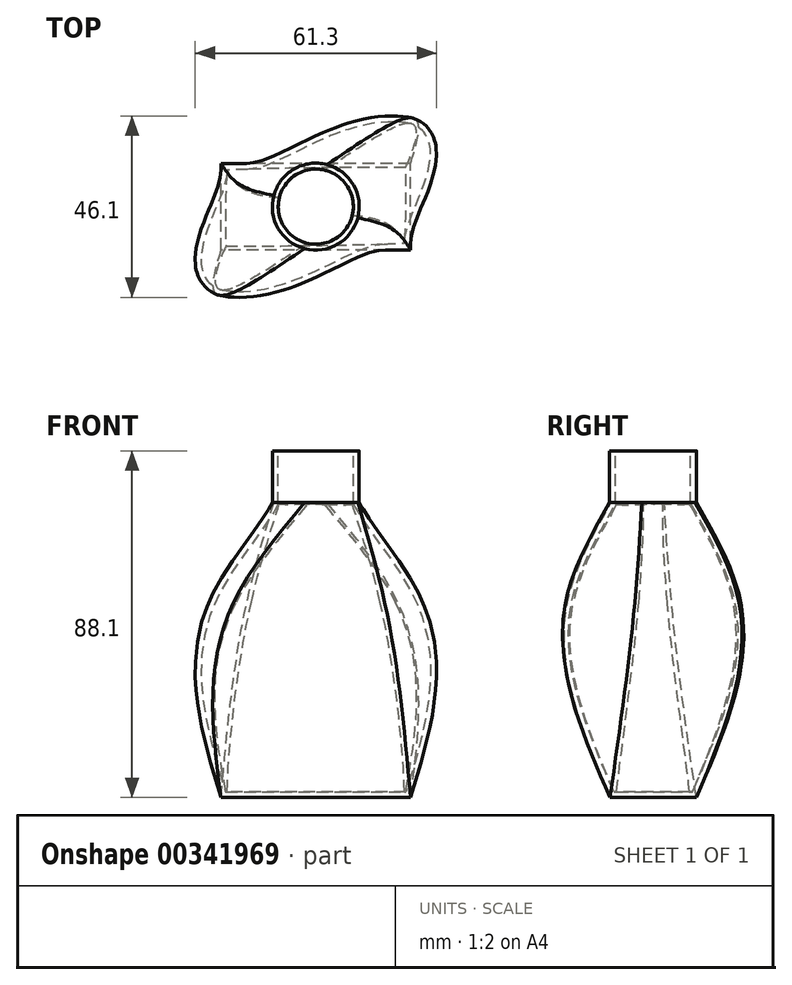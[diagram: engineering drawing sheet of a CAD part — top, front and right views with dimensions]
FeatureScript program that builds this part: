
annotation { "Feature Type Name" : "Feature", "Feature Type Description" : "" }
export const myFeature = defineFeature(function(context is Context, id is Id, definition is map)
    precondition{}
    {
        {
            var Q0;
            Q0=qCreatedBy(makeId("Top.planeOp"),FACE);
            var sketch = newSketch(context, id + "F0", { "sketchPlane" : qUnion([Q0])});
            skLineSegment(sketch, "E0.bottom", {"start": v(24.07, -10.97) * mm, "end": v(-24.07, -10.97) * mm});
            skLineSegment(sketch, "E0.top", {"start": v(24.07, 10.97) * mm, "end": v(-24.07, 10.97) * mm});
            skLineSegment(sketch, "E0.left", {"start": v(24.07, -10.97) * mm, "end": v(24.07, 10.97) * mm});
            skLineSegment(sketch, "E0.right", {"start": v(-24.07, -10.97) * mm, "end": v(-24.07, 10.97) * mm});
            skPoint(sketch, "E0.middle", {"position": v(0, 0) * mm});
            skSolve(sketch);
        }
        {
            var Q0;
            Q0=qCreatedBy(makeId("Top.planeOp"),FACE);
            cPlane(context, id + "F1", {"entities" : qUnion([Q0]), "cplaneType" : CPlaneType.OFFSET, "offset" : 50 * mm, "width" : 150 * mm, "height" : 150 * mm});
        }
        {
            var Q0;
            Q0=qCreatedBy(id+"F1.planeOp",FACE);
            var sketch = newSketch(context, id + "F2", { "sketchPlane" : qUnion([Q0])});
            skEllipse(sketch, "E1", {"center": v(0, 0) * mm, "majorRadius": 31.58 * mm, "minorRadius": 15 * mm, "majorAxis": v(0.8, 0.59)});
            skSolve(sketch);
        }
        {
            var Q0;
            Q0=qCreatedBy(id+"F1.planeOp",FACE);
            cPlane(context, id + "F3", {"entities" : qUnion([Q0]), "cplaneType" : CPlaneType.OFFSET, "offset" : 25 * mm, "width" : 150 * mm, "height" : 150 * mm});
        }
        {
            var Q0;
            Q0=qCreatedBy(id+"F3.planeOp",FACE);
            var sketch = newSketch(context, id + "F4", { "sketchPlane" : qUnion([Q0])});
            skCircle(sketch, "E2", {"center": v(0, 0) * mm, "radius": 11.04 * mm});
            skSolve(sketch);
        }
        {
            var Q0;
            Q0=makeQuery(id+"F0.imprint","IMPRINT",FACE,{"disambiguationData":[TD([[makeQuery(id+"F0.imprint","IMPRINT",EDGE,{"derivedFrom":sQuery(id+"F0.wireOp",EDGE,"E0.bottom")}),-1.0]])]});
            var Q1;
            Q1=makeQuery(id+"F2.imprint","IMPRINT",FACE,{"disambiguationData":[TD([[makeQuery(id+"F2.imprint","IMPRINT",EDGE,{"derivedFrom":sQuery(id+"F2.wireOp",EDGE,"E1")}),1.0]])]});
            var Q2;
            Q2=makeQuery(id+"F4.imprint","IMPRINT",FACE,{"disambiguationData":[TD([[makeQuery(id+"F4.imprint","IMPRINT",EDGE,{"derivedFrom":sQuery(id+"F4.wireOp",EDGE,"E2")}),1.0]])]});
            loft(context, id + "F5", {"sheetProfilesArray" : [{ "sheetProfileEntities" : qUnion([Q0]) }, { "sheetProfileEntities" : qUnion([Q1]) }, { "sheetProfileEntities" : qUnion([Q2]) }]});
        }
        {
            var Q0;
            Q0=makeQuery(id+"F5.opLoft","CAP_FACE",FACE,{"disambiguationData":[OSD([makeQuery(id+"F4.imprint","IMPRINT",FACE,{"disambiguationData":[TD([[makeQuery(id+"F4.imprint","IMPRINT",EDGE,{"derivedFrom":sQuery(id+"F4.wireOp",EDGE,"E2")}),1.0]])]})])],"isStart":true});
            extrude(context, id + "F6", {"entities" : qUnion([Q0]), "operationType" : NewBodyOperationType.ADD, "depth" : 13.1 * mm});
        }
        {
            var Q0;
            Q0=makeQuery(id+"F6.opExtrude","CAP_FACE",FACE,{"disambiguationData":[OSD([makeQuery(id+"F4.imprint","IMPRINT",FACE,{"disambiguationData":[TD([[makeQuery(id+"F4.imprint","IMPRINT",EDGE,{"derivedFrom":sQuery(id+"F4.wireOp",EDGE,"E2")}),1.0]])]})])],"isStart":false});
            shell(context, id + "F7", {"entities" : qUnion([Q0]), "thickness" : 1.5 * mm});
        }
    });
